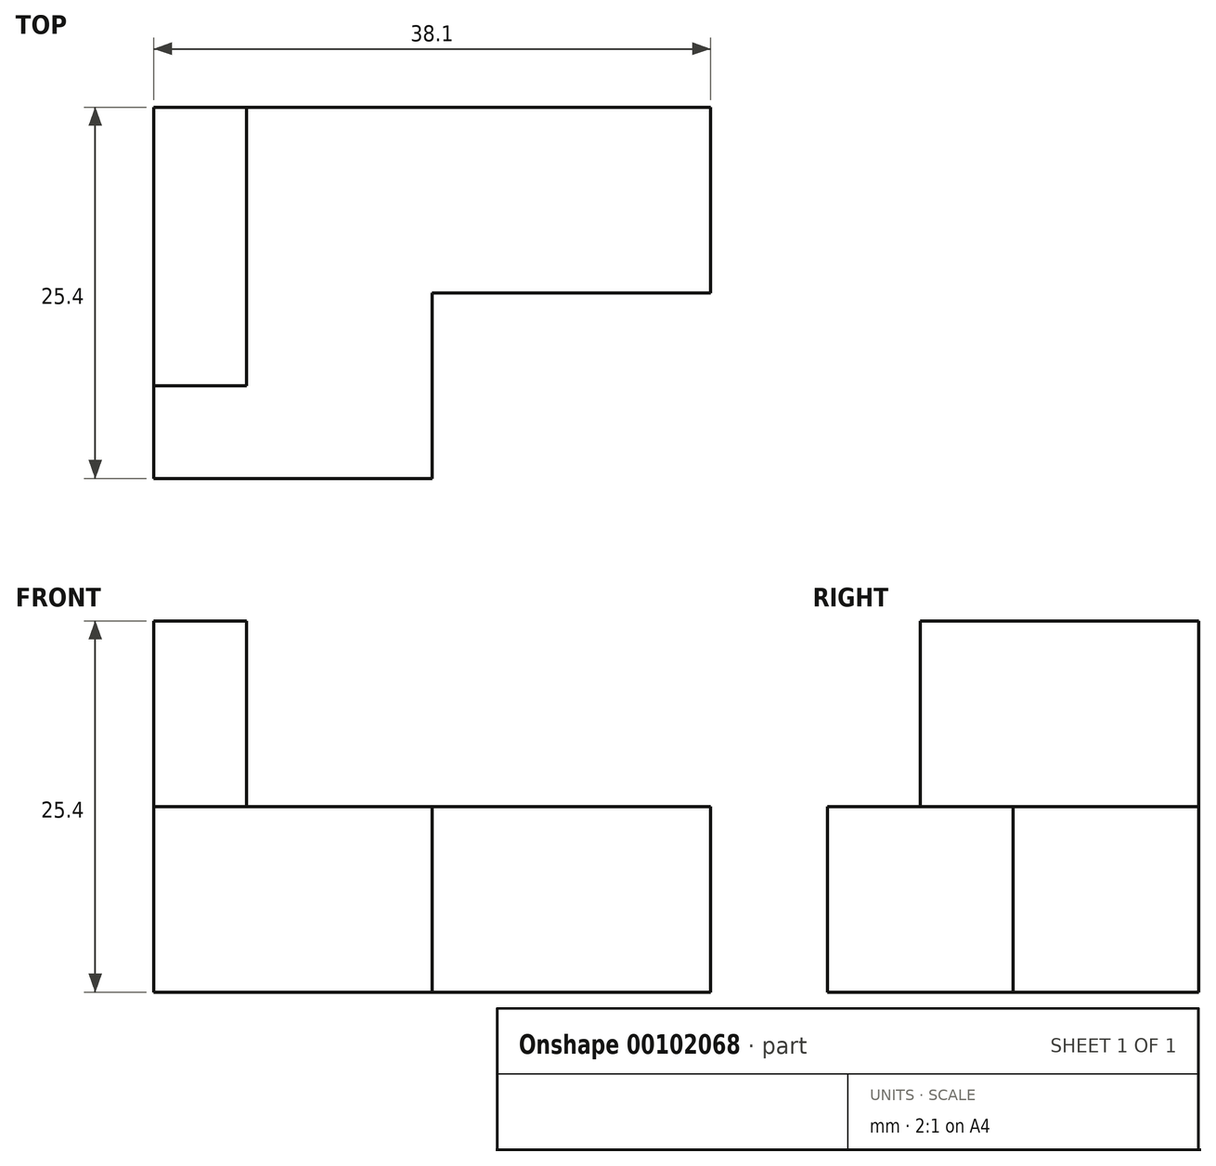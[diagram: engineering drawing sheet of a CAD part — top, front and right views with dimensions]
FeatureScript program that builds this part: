
annotation { "Feature Type Name" : "Feature", "Feature Type Description" : "" }
export const myFeature = defineFeature(function(context is Context, id is Id, definition is map)
    precondition{}
    {
        {
            var Q0;
            Q0=qCreatedBy(makeId("Front.planeOp"),FACE);
            var sketch = newSketch(context, id + "F0", { "sketchPlane" : qUnion([Q0])});
            skLineSegment(sketch, "E0", {"start": v(0, 0) * mm, "end": v(0, 12.7) * mm});
            skLineSegment(sketch, "E1", {"start": v(0, 12.7) * mm, "end": v(38.1, 12.7) * mm});
            skLineSegment(sketch, "E2", {"start": v(38.1, 12.7) * mm, "end": v(38.1, 0) * mm});
            skLineSegment(sketch, "E3", {"start": v(38.1, 0) * mm, "end": v(0, 0) * mm});
            skSolve(sketch);
        }
        {
            var Q0;
            Q0 = qSketchRegion(id + "F0", true);
            extrude(context, id + "F1", {"entities" : qUnion([Q0]), "endBound" : BoundingType.SYMMETRIC, "depth" : 25.4 * mm});
        }
        {
            var Q0;
            Q0=qCreatedBy(makeId("Top.planeOp"),FACE);
            var sketch = newSketch(context, id + "F2", { "sketchPlane" : qUnion([Q0])});
            skLineSegment(sketch, "E4", {"start": v(19.05, -12.7) * mm, "end": v(19.05, 0) * mm});
            skLineSegment(sketch, "E5", {"start": v(19.05, 0) * mm, "end": v(38.1, 0) * mm});
            skLineSegment(sketch, "E6", {"start": v(38.1, 0) * mm, "end": v(38.1, -12.7) * mm});
            skLineSegment(sketch, "E7", {"start": v(38.1, -12.7) * mm, "end": v(19.05, -12.7) * mm});
            skSolve(sketch);
        }
        {
            var Q0;
            Q0 = qSketchRegion(id + "F2", true);
            extrude(context, id + "F3", {"entities" : qUnion([Q0]), "operationType" : NewBodyOperationType.REMOVE, "endBound" : BoundingType.THROUGH_ALL, "depth" : 25.4 * mm});
        }
        {
            var Q0;
            Q0=qCreatedBy(makeId("Front.planeOp"),FACE);
            var sketch = newSketch(context, id + "F4", { "sketchPlane" : qUnion([Q0])});
            skLineSegment(sketch, "E8", {"start": v(0, 25.4) * mm, "end": v(0, 12.7) * mm});
            skLineSegment(sketch, "E9", {"start": v(0, 12.7) * mm, "end": v(0, 12.7) * mm});
            skLineSegment(sketch, "E10", {"start": v(0, 25.4) * mm, "end": v(6.35, 25.4) * mm});
            skLineSegment(sketch, "E11", {"start": v(6.35, 25.4) * mm, "end": v(6.35, 12.7) * mm});
            skLineSegment(sketch, "E12", {"start": v(6.35, 12.7) * mm, "end": v(0, 12.7) * mm});
            skSolve(sketch);
        }
        {
            var Q0;
            Q0 = qSketchRegion(id + "F4", true);
            extrude(context, id + "F5", {"entities" : qUnion([Q0]), "operationType" : NewBodyOperationType.ADD, "endBound" : BoundingType.SYMMETRIC, "depth" : 25.4 * mm});
        }
        {
            var Q0;
            Q0=qCreatedBy(makeId("Right.planeOp"),FACE);
            var sketch = newSketch(context, id + "F6", { "sketchPlane" : qUnion([Q0])});
            skLineSegment(sketch, "E13", {"start": v(-12.7, 12.7) * mm, "end": v(-12.7, 25.4) * mm});
            skLineSegment(sketch, "E14", {"start": v(-12.7, 25.4) * mm, "end": v(-6.35, 25.4) * mm});
            skLineSegment(sketch, "E15", {"start": v(-6.35, 25.4) * mm, "end": v(-6.35, 12.7) * mm});
            skLineSegment(sketch, "E16", {"start": v(-6.35, 12.7) * mm, "end": v(-12.7, 12.7) * mm});
            skSolve(sketch);
        }
        {
            var Q0;
            Q0 = qSketchRegion(id + "F6", true);
            extrude(context, id + "F7", {"entities" : qUnion([Q0]), "operationType" : NewBodyOperationType.REMOVE, "endBound" : BoundingType.THROUGH_ALL, "depth" : 25.4 * mm});
        }
    });
